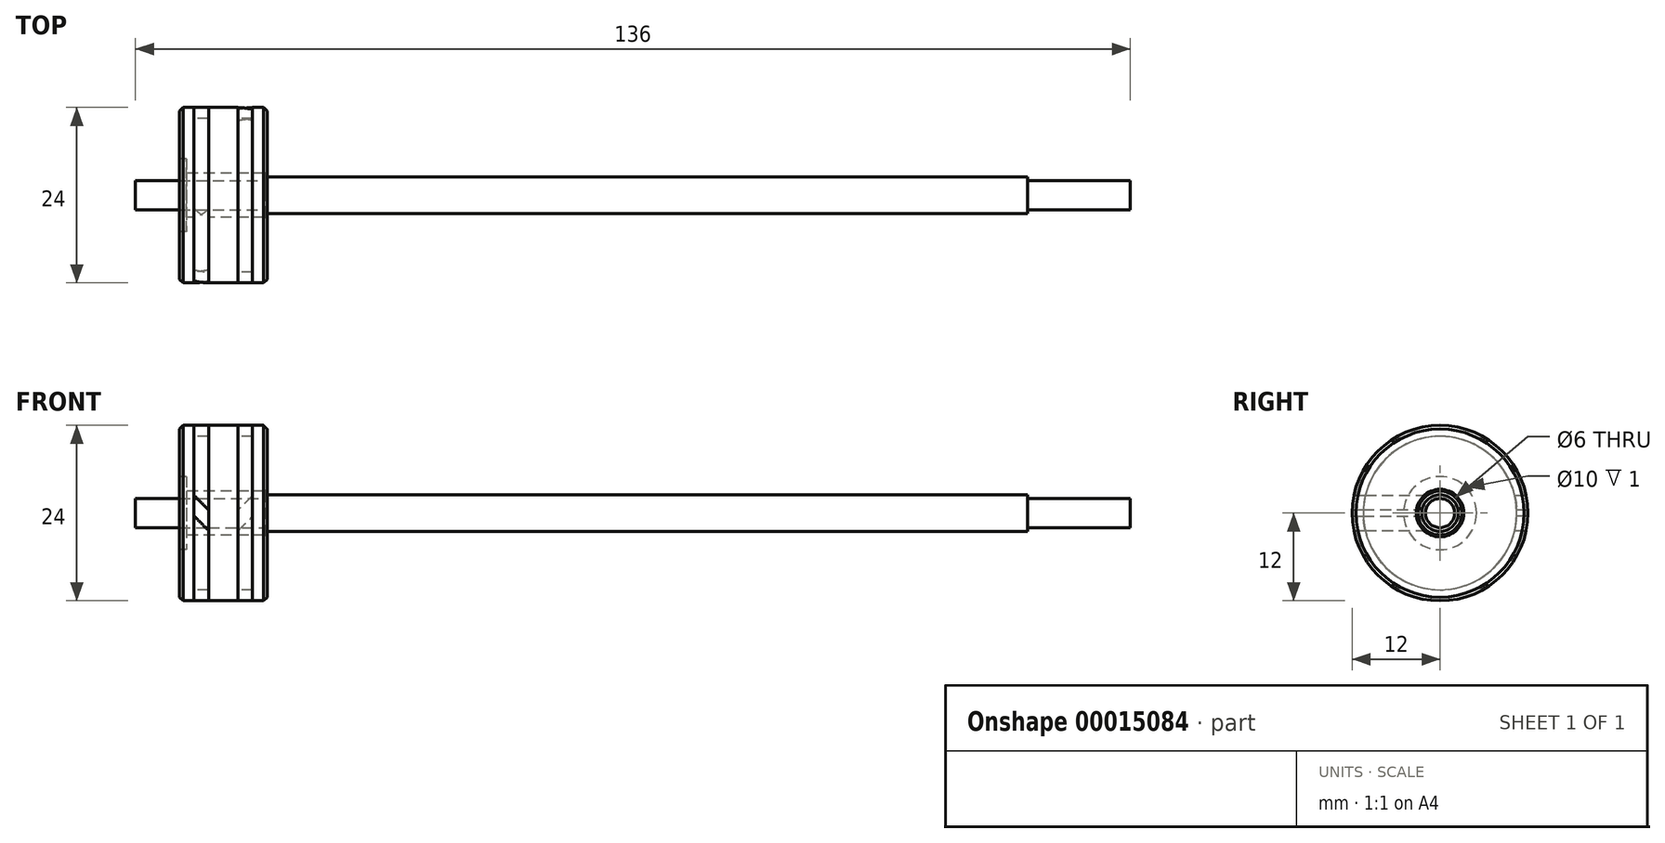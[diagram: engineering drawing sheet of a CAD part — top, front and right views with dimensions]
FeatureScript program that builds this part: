
annotation { "Feature Type Name" : "Feature", "Feature Type Description" : "" }
export const myFeature = defineFeature(function(context is Context, id is Id, definition is map)
    precondition{}
    {
        {
            var Q0;
            Q0=qCreatedBy(makeId("Front.planeOp"),FACE);
            var sketch = newSketch(context, id + "F0", { "sketchPlane" : qUnion([Q0])});
            skLineSegment(sketch, "E0", {"start": v(-16.44, 0) * mm, "end": v(15.72, 0) * mm});
            skLineSegment(sketch, "E1.rect.bottom", {"start": v(6, -12) * mm, "end": v(-6, -12) * mm});
            skLineSegment(sketch, "E1.rect.top", {"start": v(6, 12) * mm, "end": v(4, 12) * mm});
            skLineSegment(sketch, "E1.rect.left", {"start": v(6, -12) * mm, "end": v(6, -3) * mm});
            skLineSegment(sketch, "E1.rect.right", {"start": v(-6, -12) * mm, "end": v(-6, -5) * mm});
            skPoint(sketch, "E1.rect.middle", {"position": v(0, 0) * mm});
            skLineSegment(sketch, "E2.rect.bottom", {"start": v(-5, 5) * mm, "end": v(-6, 5) * mm});
            skLineSegment(sketch, "E2.rect.top", {"start": v(-5, -5) * mm, "end": v(-6, -5) * mm});
            skLineSegment(sketch, "E2.rect.left", {"start": v(-5, 5) * mm, "end": v(-5, 3) * mm});
            skPoint(sketch, "E2.rect.middle", {"position": v(-6, 0) * mm});
            skLineSegment(sketch, "E3.rect.bottom", {"start": v(-5, 3) * mm, "end": v(5, 3) * mm});
            skLineSegment(sketch, "E3.rect.top", {"start": v(-5, -3) * mm, "end": v(5, -3) * mm});
            skLineSegment(sketch, "E4.rect.bottom", {"start": v(6, 3) * mm, "end": v(4, 3) * mm});
            skLineSegment(sketch, "E4.rect.top", {"start": v(6, 3) * mm, "end": v(4, 3) * mm});
            skLineSegment(sketch, "E4.rect.left", {"start": v(6, 3) * mm, "end": v(6, 3) * mm});
            skLineSegment(sketch, "E4.rect.right", {"start": v(4, 3) * mm, "end": v(4, 3) * mm});
            skPoint(sketch, "E4.rect.middle", {"position": v(5, 3) * mm});
            skLineSegment(sketch, "E5.rect.bottom", {"start": v(6, -3) * mm, "end": v(4, -3) * mm});
            skLineSegment(sketch, "E5.rect.top", {"start": v(6, -3) * mm, "end": v(4, -3) * mm});
            skLineSegment(sketch, "E5.rect.left", {"start": v(6, -3) * mm, "end": v(6, -3) * mm});
            skLineSegment(sketch, "E5.rect.right", {"start": v(4, -3) * mm, "end": v(4, -3) * mm});
            skPoint(sketch, "E5.rect.middle", {"position": v(5, -3) * mm});
            skLineSegment(sketch, "E6.rect.bottom", {"start": v(-2, 10.5) * mm, "end": v(-4, 10.5) * mm});
            skLineSegment(sketch, "E6.rect.left", {"start": v(-2, 10.5) * mm, "end": v(-2, 12) * mm});
            skLineSegment(sketch, "E6.rect.right", {"start": v(-4, 10.5) * mm, "end": v(-4, 12) * mm});
            skPoint(sketch, "E6.rect.middle", {"position": v(-3, 12) * mm});
            skLineSegment(sketch, "E7.rect.bottom", {"start": v(4, 10.5) * mm, "end": v(2, 10.5) * mm});
            skLineSegment(sketch, "E7.rect.left", {"start": v(4, 10.5) * mm, "end": v(4, 12) * mm});
            skLineSegment(sketch, "E7.rect.right", {"start": v(2, 10.5) * mm, "end": v(2, 12) * mm});
            skPoint(sketch, "E7.rect.middle", {"position": v(3, 12) * mm});
            skPoint(sketch, "E8.orphan", {"position": v(-7, 5) * mm});
            skPoint(sketch, "E9.orphan", {"position": v(-7, -5) * mm});
            skLineSegment(sketch, "E10.trimOffspring", {"start": v(-6, 5) * mm, "end": v(-6, 12) * mm});
            skLineSegment(sketch, "E11.trimOffspring", {"start": v(-5, -3) * mm, "end": v(-5, -5) * mm});
            skLineSegment(sketch, "E12.trimOffspring", {"start": v(6, 3) * mm, "end": v(6, 12) * mm});
            skLineSegment(sketch, "E13", {"start": v(-6, 10.5) * mm, "end": v(6, 10.5) * mm, "construction": true});
            skLineSegment(sketch, "E14.0.MirrorCS", {"start": v(-6, -10.5) * mm, "end": v(6, -10.5) * mm, "construction": true});
            skLineSegment(sketch, "E15", {"start": v(0, 12) * mm, "end": v(0, 3) * mm, "construction": true});
            skPoint(sketch, "E6.rect.top.end.orphan", {"position": v(-4, 13.5) * mm});
            skPoint(sketch, "E16.orphan", {"position": v(-2, 13.5) * mm});
            skPoint(sketch, "E7.rect.top.end.orphan", {"position": v(2, 13.5) * mm});
            skPoint(sketch, "E17.orphan", {"position": v(4, 13.5) * mm});
            skLineSegment(sketch, "E18.trimOffspring", {"start": v(2, 12) * mm, "end": v(-2, 12) * mm});
            skLineSegment(sketch, "E19.trimOffspring", {"start": v(-4, 12) * mm, "end": v(-6, 12) * mm});
            skSolve(sketch);
        }
        {
            var Q0;
            Q0=makeQuery(id+"F0.imprint","IMPRINT",FACE,{"disambiguationData":[TD([[makeQuery(id+"F0.imprint","IMPRINT",EDGE,{"derivedFrom":sQuery(id+"F0.wireOp",EDGE,"E1.rect.top")}),1.0]])]});
            var Q1;
            Q1=sQuery(id+"F0.wireOp",EDGE,"E0");
            revolve(context, id + "F1", {"entities" : qUnion([Q0]), "axis" : qUnion([Q1]), "revolveType" : RevolveType.FULL});
        }
        {
            var Q0;
            Q0=makeQuery(id+"F1.opRevolve","SWEPT_EDGE",EDGE,{"disambiguationData":[OSD([sQuery(id+"F0.wireOp",EDGE,"E10.trimOffspring"),sQuery(id+"F0.wireOp",EDGE,"E19.trimOffspring")])]});
            var Q1;
            Q1=makeQuery(id+"F1.opRevolve","SWEPT_EDGE",EDGE,{"disambiguationData":[OSD([sQuery(id+"F0.wireOp",EDGE,"E1.rect.top"),sQuery(id+"F0.wireOp",EDGE,"E12.trimOffspring")])]});
            chamfer(context, id + "F2", {"entities" : qUnion([Q0, Q1]), "width" : .5 * mm, "tangentPropagation" : true});
        }
        {
            var Q0;
            Q0=makeQuery(id+"F1.opRevolve","SWEPT_EDGE",EDGE,{"disambiguationData":[OSD([sQuery(id+"F0.wireOp",EDGE,"E4.rect.top"),sQuery(id+"F0.wireOp",EDGE,"E12.trimOffspring")])]});
            chamfer(context, id + "F3", {"entities" : qUnion([Q0]), "width" : .25 * mm, "tangentPropagation" : true});
        }
        {
            var Q0;
            Q0=makeQuery(id+"F1.opRevolve","SWEPT_FACE",FACE,{"disambiguationData":[OSD([sQuery(id+"F0.wireOp",EDGE,"E6.rect.right")])]});
            var sketch = newSketch(context, id + "F4", { "sketchPlane" : qUnion([Q0])});
            skCircle(sketch, "E20.0", {"center": v(0, 0) * mm, "radius": 12 * mm});
            skCircle(sketch, "E21.0", {"center": v(0, 0) * mm, "radius": 10.5 * mm});
            skSolve(sketch);
        }
        {
            var Q0;
            Q0=makeQuery(id+"F4.imprint","IMPRINT",FACE,{"disambiguationData":[TD([[makeQuery(id+"F4.imprint","IMPRINT",EDGE,{"derivedFrom":sQuery(id+"F4.wireOp",EDGE,"E20.0")}),-1.0]])]});
            extrude(context, id + "F5", {"entities" : qUnion([Q0]), "depth" : 2 * mm});
        }
        {
            var Q0;
            Q0=qCreatedBy(makeId("Front.planeOp"),FACE);
            var sketch = newSketch(context, id + "F6", { "sketchPlane" : qUnion([Q0])});
            skLineSegment(sketch, "E22", {"start": v(0, 0) * mm, "end": v(-10.1, 0) * mm, "construction": true});
            skLineSegment(sketch, "E23", {"start": v(-2, -2.39) * mm, "end": v(-4, -0.39) * mm});
            skLineSegment(sketch, "E24.0", {"start": v(-4, -12) * mm, "end": v(-4, 12) * mm});
            skLineSegment(sketch, "E25.0", {"start": v(-2, -12) * mm, "end": v(-2, 12) * mm});
            skLineSegment(sketch, "E26", {"start": v(-4, 2.44) * mm, "end": v(-2, 0.44) * mm});
            skSolve(sketch);
        }
        {
            var Q0;
            {var subQ2=sQuery(id+"F6.wireOp",EDGE,"E23");Q0=makeQuery(id+"F6.imprint","IMPRINT",FACE,{"disambiguationData":[TD([[makeQuery(id+"F6.imprint","IMPRINT",EDGE,{"derivedFrom":subQ2}),-1.0]])]});}
            extrude(context, id + "F7", {"entities" : qUnion([Q0]), "operationType" : NewBodyOperationType.REMOVE, "endBound" : BoundingType.THROUGH_ALL, "depth" : 25 * mm});
        }
        {
            var Q0;
            Q0=makeQuery(id+"F5.opExtrude","SWEPT_BODY",BODY,{"disambiguationData":[OSD([sQuery(id+"F4.wireOp",EDGE,"E20.0"),sQuery(id+"F4.wireOp",EDGE,"E21.0")])]});
            transform(context, id + "F8", {"entities" : qUnion([Q0]), "transformType" : TransformType.TRANSLATION_3D, "dx" : 6 * mm, "dy" : 0 * mm, "dz" : 0 * mm, "makeCopy" : true});
        }
        {
            var Q0;
            Q0=makeQuery(id+"F8.opPattern","COPY",BODY,{"derivedFrom":makeQuery(id+"F5.opExtrude","SWEPT_BODY",BODY,{"disambiguationData":[OSD([sQuery(id+"F4.wireOp",EDGE,"E20.0"),sQuery(id+"F4.wireOp",EDGE,"E21.0")])]}),"instanceName":"1"});
            var Q1;
            {var subQ0=sQuery(id+"F0.wireOp",EDGE,"E12.trimOffspring");Q1=makeQuery(id+"F2.opChamfer","BLEND_EDGE",EDGE,{"blendedFrom":[makeQuery(id+"F1.opRevolve","SWEPT_EDGE",EDGE,{"disambiguationData":[OSD([sQuery(id+"F0.wireOp",EDGE,"E1.rect.top"),subQ0])]}),makeQuery(id+"F1.opRevolve","SWEPT_FACE",FACE,{"disambiguationData":[OSD([subQ0])]})],"blendedInto":[makeQuery(id+"F1.opRevolve","SWEPT_FACE",FACE,{"disambiguationData":[OSD([subQ0])]})]});}
            transform(context, id + "F9", {"entities" : qUnion([Q0]), "transformType" : TransformType.ROTATION, "transformAxis" : qUnion([Q1]), "angle" : 180 * degree, "makeCopy" : false});
        }
        {
            var Q0;
            Q0=makeQuery(id+"F1.opRevolve","SWEPT_FACE",FACE,{"disambiguationData":[OSD([sQuery(id+"F0.wireOp",EDGE,"E12.trimOffspring")])]});
            var sketch = newSketch(context, id + "F10", { "sketchPlane" : qUnion([Q0])});
            skCircle(sketch, "E27.0", {"center": v(0, 0) * mm, "radius": 3 * mm});
            skCircle(sketch, "E28", {"center": v(0, 0) * mm, "radius": 2 * mm});
            skSolve(sketch);
        }
        {
            var Q0;
            Q0=makeQuery(id+"F10.imprint","IMPRINT",FACE,{"disambiguationData":[TD([[makeQuery(id+"F10.imprint","IMPRINT",EDGE,{"derivedFrom":sQuery(id+"F10.wireOp",EDGE,"E28")}),1.0]])]});
            extrude(context, id + "F11", {"entities" : qUnion([Q0]), "oppositeDirection" : true, "depth" : 18 * mm});
        }
        {
            var Q0;
            Q0=makeQuery(id+"F11.opExtrude","CAP_FACE",FACE,{"disambiguationData":[OSD([sQuery(id+"F10.wireOp",EDGE,"E28")])],"isStart":true});
            var sketch = newSketch(context, id + "F12", { "sketchPlane" : qUnion([Q0])});
            skCircle(sketch, "E29.0", {"center": v(0, 0) * mm, "radius": 2 * mm});
            skCircle(sketch, "E30", {"center": v(0, 0) * mm, "radius": 2.5 * mm});
            skSolve(sketch);
        }
        {
            var Q0;
            Q0=makeQuery(id+"F12.imprint","IMPRINT",FACE,{"disambiguationData":[TD([[makeQuery(id+"F12.imprint","IMPRINT",EDGE,{"derivedFrom":sQuery(id+"F12.wireOp",EDGE,"E29.0")}),1.0]])]});
            var Q1;
            Q1=makeQuery(id+"F12.imprint","IMPRINT",FACE,{"disambiguationData":[TD([[makeQuery(id+"F12.imprint","IMPRINT",EDGE,{"derivedFrom":sQuery(id+"F12.wireOp",EDGE,"E29.0")}),-1.0]])]});
            extrude(context, id + "F13", {"entities" : qUnion([Q0, Q1]), "operationType" : NewBodyOperationType.ADD, "depth" : (124 - 10 - 10) * mm});
        }
        {
            var Q0;
            Q0=makeQuery(id+"F13.opExtrude","CAP_FACE",FACE,{"disambiguationData":[OSD([sQuery(id+"F12.wireOp",EDGE,"E30")])],"isStart":false});
            var sketch = newSketch(context, id + "F14", { "sketchPlane" : qUnion([Q0])});
            skCircle(sketch, "E31.0", {"center": v(0, 0) * mm, "radius": 2.5 * mm});
            skCircle(sketch, "E32", {"center": v(0, 0) * mm, "radius": 2 * mm});
            skSolve(sketch);
        }
        {
            var Q0;
            Q0=makeQuery(id+"F14.imprint","IMPRINT",FACE,{"disambiguationData":[TD([[makeQuery(id+"F14.imprint","IMPRINT",EDGE,{"derivedFrom":sQuery(id+"F14.wireOp",EDGE,"E32")}),1.0]])]});
            var Q1;
            Q1=sQuery(id+"F14.wireOp",EDGE,"E32");
            extrude(context, id + "F15", {"entities" : qUnion([Q0]), "operationType" : NewBodyOperationType.ADD, "surfaceEntities" : qUnion([Q1]), "depth" : 14 * mm});
        }
    });
